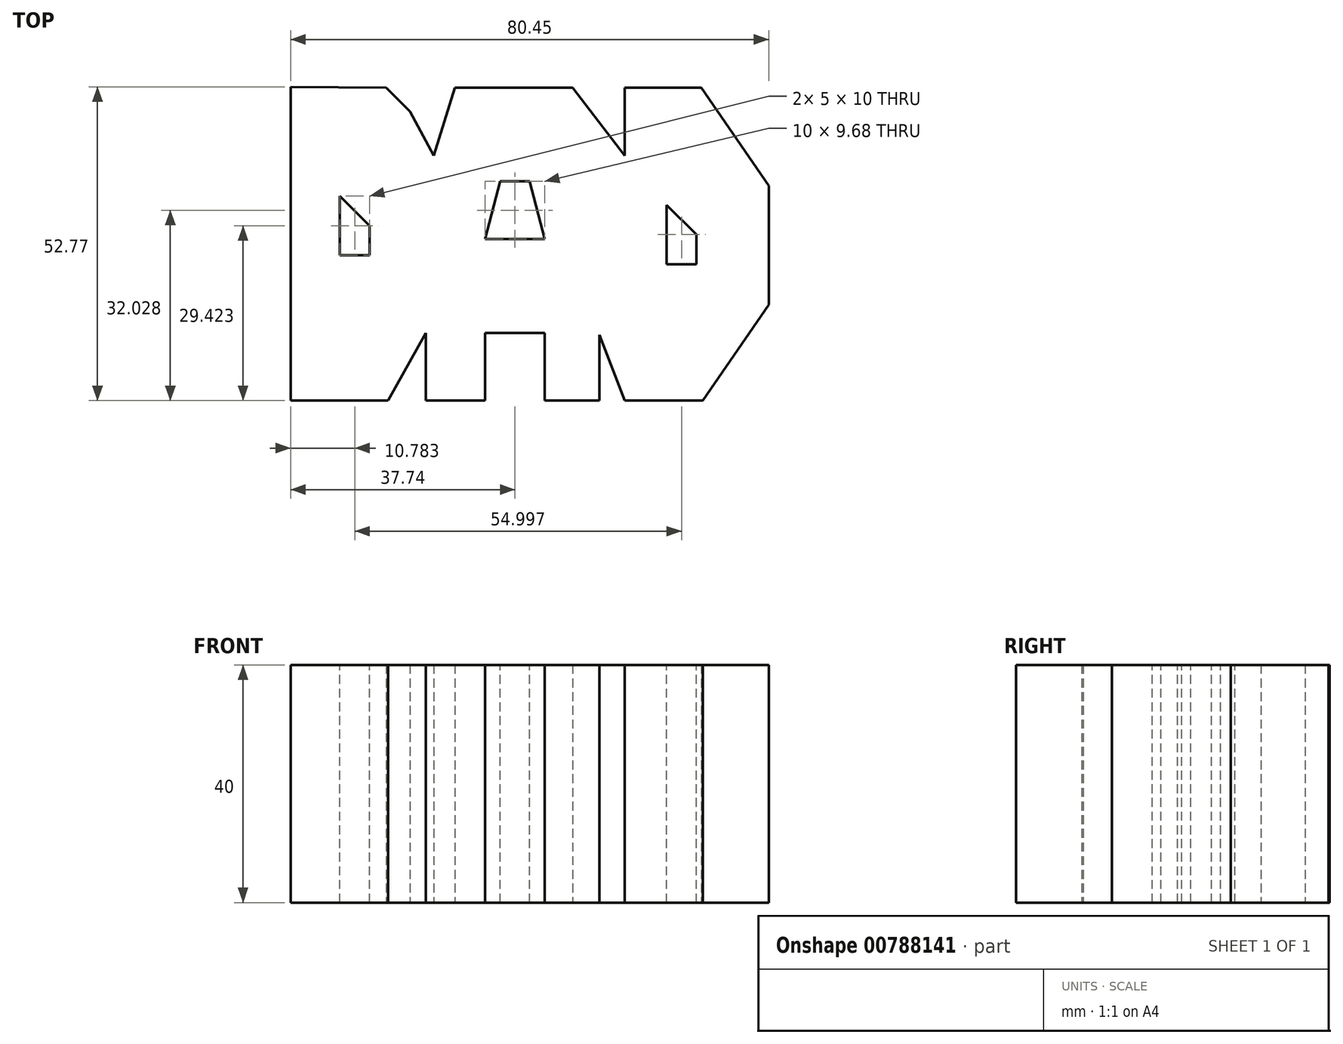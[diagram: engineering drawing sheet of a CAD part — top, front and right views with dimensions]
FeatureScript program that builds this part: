
annotation { "Feature Type Name" : "Feature", "Feature Type Description" : "" }
export const myFeature = defineFeature(function(context is Context, id is Id, definition is map)
    precondition{}
    {
        {
            var Q0;
            Q0=qCreatedBy(makeId("Top.planeOp"),FACE);
            var sketch = newSketch(context, id + "F0", { "sketchPlane" : qUnion([Q0])});
            skLineSegment(sketch, "E0.bottom", {"start": v(-30.25, 38.59) * mm, "end": v(34.75, 38.59) * mm});
            skLineSegment(sketch, "E0.top", {"start": v(-30.25, -1.41) * mm, "end": v(34.75, -1.41) * mm});
            skLineSegment(sketch, "E0.left", {"start": v(-30.25, 38.59) * mm, "end": v(-30.25, -1.41) * mm});
            skLineSegment(sketch, "E0.right", {"start": v(34.75, 38.59) * mm, "end": v(34.75, -1.41) * mm});
            skSolve(sketch);
        }
        {
            var Q0;
            Q0=makeQuery(id+"F0.imprint","IMPRINT",FACE,{"disambiguationData":[TD([[makeQuery(id+"F0.imprint","IMPRINT",EDGE,{"derivedFrom":sQuery(id+"F0.wireOp",EDGE,"E0.bottom")}),-1.0]])]});
            var sketch = newSketch(context, id + "F1", { "sketchPlane" : qUnion([Q0])});
            skLineSegment(sketch, "E1", {"start": v(-42.74, 52.77) * mm, "end": v(-42.74, 0) * mm});
            skLineSegment(sketch, "E2", {"start": v(-42.74, 0) * mm, "end": v(-26.36, 0) * mm});
            skLineSegment(sketch, "E3", {"start": v(-26.36, 0) * mm, "end": v(-20, 11.34) * mm});
            skLineSegment(sketch, "E4", {"start": v(-20, 11.34) * mm, "end": v(-20, 0) * mm});
            skLineSegment(sketch, "E5", {"start": v(-20, 0) * mm, "end": v(-10, 0) * mm});
            skLineSegment(sketch, "E6", {"start": v(-10, 0) * mm, "end": v(-10, 11.34) * mm});
            skLineSegment(sketch, "E7", {"start": v(-10, 11.34) * mm, "end": v(0, 11.34) * mm});
            skLineSegment(sketch, "E8", {"start": v(0, 11.34) * mm, "end": v(0, 0) * mm});
            skLineSegment(sketch, "E9", {"start": v(0, 0) * mm, "end": v(9.2, 0) * mm});
            skLineSegment(sketch, "E10", {"start": v(9.2, 0) * mm, "end": v(9.2, 11.05) * mm});
            skLineSegment(sketch, "E11", {"start": v(9.2, 11.05) * mm, "end": v(13.48, 0) * mm});
            skLineSegment(sketch, "E12", {"start": v(13.48, 0) * mm, "end": v(26.65, 0) * mm});
            skLineSegment(sketch, "E13", {"start": v(26.65, 0) * mm, "end": v(37.7, 16.12) * mm});
            skLineSegment(sketch, "E14", {"start": v(37.7, 16.12) * mm, "end": v(37.7, 36.12) * mm});
            skLineSegment(sketch, "E15", {"start": v(37.7, 36.12) * mm, "end": v(26.4, 52.62) * mm});
            skLineSegment(sketch, "E16", {"start": v(26.4, 52.62) * mm, "end": v(13.48, 52.62) * mm});
            skLineSegment(sketch, "E17", {"start": v(13.48, 52.62) * mm, "end": v(13.48, 41.23) * mm});
            skLineSegment(sketch, "E18", {"start": v(13.48, 41.23) * mm, "end": v(4.73, 52.63) * mm});
            skLineSegment(sketch, "E19", {"start": v(4.73, 52.63) * mm, "end": v(-15.07, 52.63) * mm});
            skLineSegment(sketch, "E20", {"start": v(-15.07, 52.63) * mm, "end": v(-18.68, 41.23) * mm});
            skLineSegment(sketch, "E21", {"start": v(-18.68, 41.23) * mm, "end": v(-22.64, 48.65) * mm});
            skLineSegment(sketch, "E22", {"start": v(-22.64, 48.65) * mm, "end": v(-26.63, 52.63) * mm});
            skLineSegment(sketch, "E23", {"start": v(-26.63, 52.63) * mm, "end": v(-42.74, 52.77) * mm});
            skSolve(sketch);
        }
        {
            var Q0;
            {var subQ4=sQuery(id+"F1.wireOp",EDGE,"E3");Q0=makeQuery(id+"F1.imprint","IMPRINT",FACE,{"disambiguationData":[TD([[makeQuery(id+"F1.imprint","IMPRINT",EDGE,{"derivedFrom":subQ4}),1.0]])]});}
            var Q1;
            {var subQ0=sQuery(id+"F1.wireOp",EDGE,"E1");Q1=makeQuery(id+"F1.imprint","IMPRINT",FACE,{"disambiguationData":[TD([[makeQuery(id+"F1.imprint","IMPRINT",EDGE,{"derivedFrom":subQ0}),1.0]])]});}
            extrude(context, id + "F2", {"entities" : qUnion([Q0, Q1]), "depth" : 40 * mm, "offsetDistance" : 25 * mm});
        }
        {
            var Q0;
            Q0=makeQuery(id+"F2.opExtrude","CAP_FACE",FACE,{"disambiguationData":[OSD([sQuery(id+"F1.wireOp",EDGE,"E1"),sQuery(id+"F1.wireOp",EDGE,"E2"),sQuery(id+"F1.wireOp",EDGE,"E3"),sQuery(id+"F1.wireOp",EDGE,"E4"),sQuery(id+"F1.wireOp",EDGE,"E5"),sQuery(id+"F1.wireOp",EDGE,"E6"),sQuery(id+"F1.wireOp",EDGE,"E7"),sQuery(id+"F1.wireOp",EDGE,"E8"),sQuery(id+"F1.wireOp",EDGE,"E9"),sQuery(id+"F1.wireOp",EDGE,"E10"),sQuery(id+"F1.wireOp",EDGE,"E11"),sQuery(id+"F1.wireOp",EDGE,"E12"),sQuery(id+"F1.wireOp",EDGE,"E13"),sQuery(id+"F1.wireOp",EDGE,"E14"),sQuery(id+"F1.wireOp",EDGE,"E15"),sQuery(id+"F1.wireOp",EDGE,"E16"),sQuery(id+"F1.wireOp",EDGE,"E17"),sQuery(id+"F1.wireOp",EDGE,"E18"),sQuery(id+"F1.wireOp",EDGE,"E19"),sQuery(id+"F1.wireOp",EDGE,"E20"),sQuery(id+"F1.wireOp",EDGE,"E21"),sQuery(id+"F1.wireOp",EDGE,"E22"),sQuery(id+"F1.wireOp",EDGE,"E23")])],"isStart":false});
            var sketch = newSketch(context, id + "F3", { "sketchPlane" : qUnion([Q0])});
            skLineSegment(sketch, "E24", {"start": v(-34.46, 34.42) * mm, "end": v(-34.46, 24.42) * mm});
            skLineSegment(sketch, "E25", {"start": v(-34.46, 24.42) * mm, "end": v(-29.46, 24.42) * mm});
            skLineSegment(sketch, "E26", {"start": v(-29.46, 24.42) * mm, "end": v(-29.46, 29.42) * mm});
            skLineSegment(sketch, "E27", {"start": v(-29.46, 29.42) * mm, "end": v(-34.46, 34.42) * mm});
            skSolve(sketch);
        }
        {
            var Q0;
            Q0=makeQuery(id+"F3.imprint","IMPRINT",FACE,{"disambiguationData":[TD([[makeQuery(id+"F3.imprint","IMPRINT",EDGE,{"derivedFrom":sQuery(id+"F3.wireOp",EDGE,"E24")}),-1.0]])]});
            var sketch = newSketch(context, id + "F4", { "sketchPlane" : qUnion([Q0])});
            skLineSegment(sketch, "E28", {"start": v(-10, 27.19) * mm, "end": v(0, 27.19) * mm});
            skLineSegment(sketch, "E29", {"start": v(0, 27.19) * mm, "end": v(-2.5, 36.87) * mm});
            skLineSegment(sketch, "E30", {"start": v(-2.5, 36.87) * mm, "end": v(-7.5, 36.87) * mm});
            skLineSegment(sketch, "E31", {"start": v(-7.5, 36.87) * mm, "end": v(-10, 27.19) * mm});
            skSolve(sketch);
        }
        {
            var Q0;
            Q0=makeQuery(id+"F3.imprint","IMPRINT",FACE,{"disambiguationData":[TD([[makeQuery(id+"F3.imprint","IMPRINT",EDGE,{"derivedFrom":sQuery(id+"F3.wireOp",EDGE,"E24")}),-1.0]])]});
            var sketch = newSketch(context, id + "F5", { "sketchPlane" : qUnion([Q0])});
            skLineSegment(sketch, "E32", {"start": v(20.54, 32.92) * mm, "end": v(20.54, 22.92) * mm});
            skLineSegment(sketch, "E33", {"start": v(20.54, 22.92) * mm, "end": v(25.54, 22.92) * mm});
            skLineSegment(sketch, "E34", {"start": v(25.54, 22.92) * mm, "end": v(25.54, 27.92) * mm});
            skLineSegment(sketch, "E35", {"start": v(25.54, 27.92) * mm, "end": v(20.54, 32.92) * mm});
            skSolve(sketch);
        }
        {
            var Q0;
            Q0=makeQuery(id+"F5.imprint","IMPRINT",FACE,{"disambiguationData":[TD([[makeQuery(id+"F5.imprint","IMPRINT",EDGE,{"derivedFrom":makeQuery(id+"F3.imprint","IMPRINT",EDGE,{"derivedFrom":sQuery(id+"F3.wireOp",EDGE,"E24")})}),1.0]])]});
            var Q1;
            Q1=makeQuery(id+"F5.imprint","IMPRINT",FACE,{"disambiguationData":[TD([[makeQuery(id+"F5.imprint","IMPRINT",EDGE,{"derivedFrom":sQuery(id+"F5.wireOp",EDGE,"E32")}),1.0]])]});
            extrude(context, id + "F6", {"entities" : qUnion([Q0, Q1]), "operationType" : NewBodyOperationType.REMOVE, "endBound" : BoundingType.THROUGH_ALL, "oppositeDirection" : true, "depth" : 25 * mm, "offsetDistance" : 25 * mm});
        }
        {
            var Q0;
            Q0=makeQuery(id+"F4.imprint","IMPRINT",FACE,{"disambiguationData":[TD([[makeQuery(id+"F4.imprint","IMPRINT",EDGE,{"derivedFrom":sQuery(id+"F4.wireOp",EDGE,"E28")}),1.0]])]});
            extrude(context, id + "F7", {"entities" : qUnion([Q0]), "operationType" : NewBodyOperationType.REMOVE, "endBound" : BoundingType.THROUGH_ALL, "oppositeDirection" : true, "depth" : 25 * mm, "offsetDistance" : 25 * mm});
        }
    });
